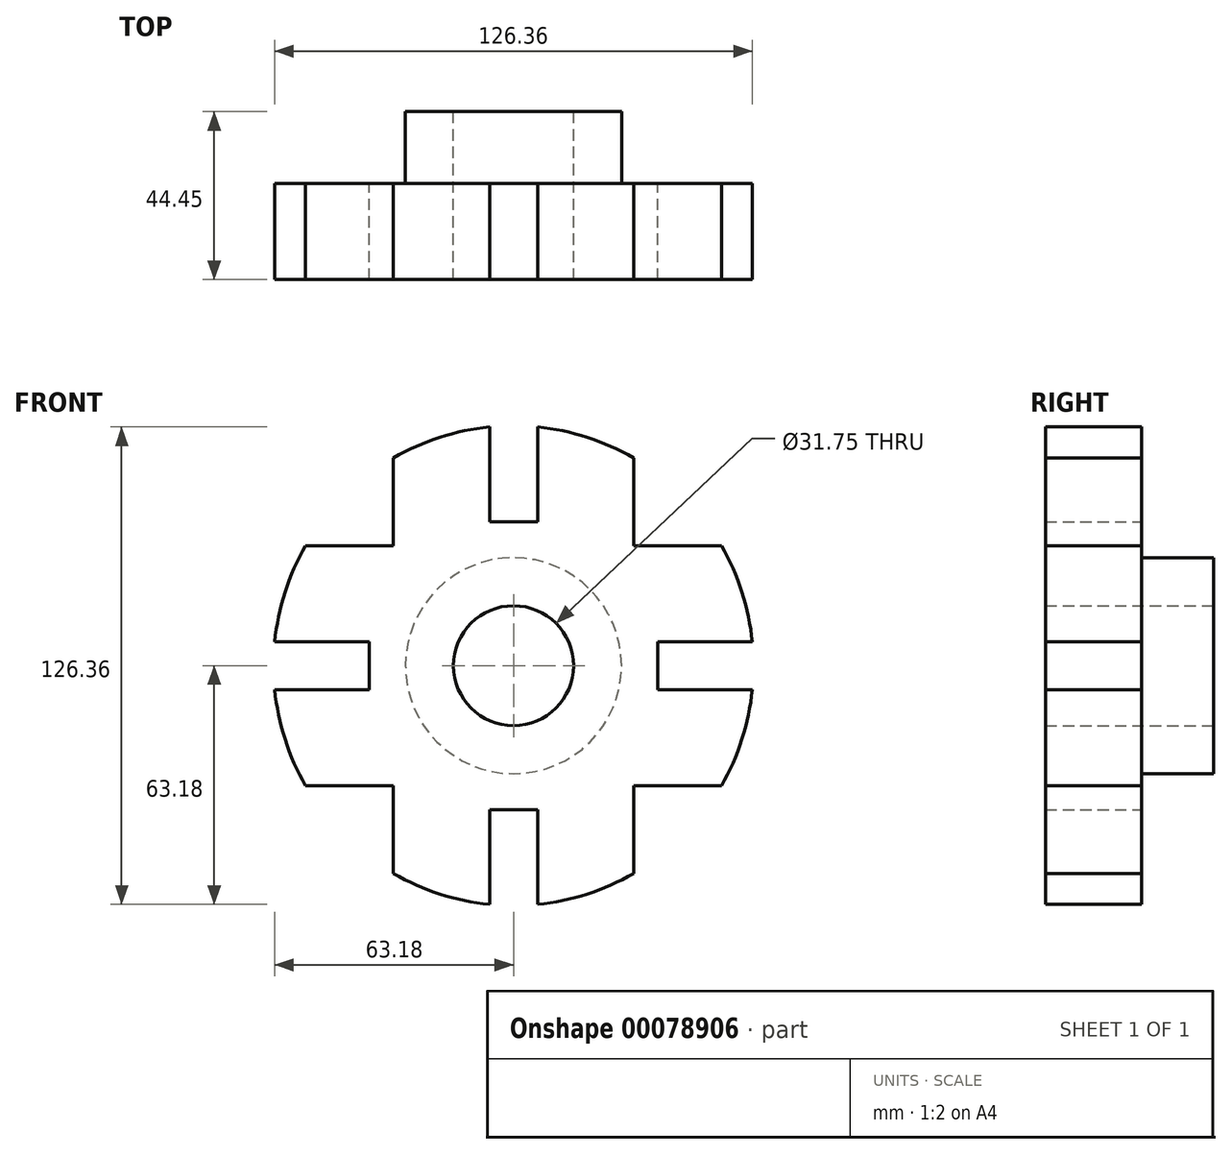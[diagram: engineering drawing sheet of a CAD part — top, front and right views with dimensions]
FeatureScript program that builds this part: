
annotation { "Feature Type Name" : "Feature", "Feature Type Description" : "" }
export const myFeature = defineFeature(function(context is Context, id is Id, definition is map)
    precondition{}
    {
        {
            var Q0;
            Q0=qCreatedBy(makeId("Front.planeOp"),FACE);
            var sketch = newSketch(context, id + "F0", { "sketchPlane" : qUnion([Q0])});
            skCircle(sketch, "E0", {"center": v(0, 0) * mm, "radius": 15.88 * mm});
            skCircle(sketch, "E1", {"center": v(0, 0) * mm, "radius": 28.58 * mm});
            skArc(sketch, "E2", {"start": v(63.18, 6.35) * mm, "mid": v(60.44, 19.49) * mm, "end": v(55, 31.75) * mm});
            skLineSegment(sketch, "E3", {"start": v(0, 38.1) * mm, "end": v(0, 0) * mm, "construction": true});
            skLineSegment(sketch, "E4", {"start": v(0, -28.58) * mm, "end": v(0, 0) * mm, "construction": true});
            skLineSegment(sketch, "E5", {"start": v(38.1, 0) * mm, "end": v(0, 0) * mm, "construction": true});
            skLineSegment(sketch, "E6", {"start": v(0, 0) * mm, "end": v(-28.58, 0) * mm, "construction": true});
            skLineSegment(sketch, "E7", {"start": v(0, 38.1) * mm, "end": v(6.35, 38.1) * mm});
            skLineSegment(sketch, "E8", {"start": v(6.35, 38.1) * mm, "end": v(6.35, 63.18) * mm});
            skLineSegment(sketch, "E9", {"start": v(31.75, 55) * mm, "end": v(31.75, 31.75) * mm});
            skLineSegment(sketch, "E10", {"start": v(31.75, 31.75) * mm, "end": v(55, 31.75) * mm});
            skLineSegment(sketch, "E11", {"start": v(38.1, 0) * mm, "end": v(38.1, 6.35) * mm});
            skLineSegment(sketch, "E12", {"start": v(38.1, 6.35) * mm, "end": v(63.18, 6.35) * mm});
            skPoint(sketch, "E13.orphan", {"position": v(0, -63.5) * mm});
            skArc(sketch, "E14.trimOffspring", {"start": v(31.75, 55) * mm, "mid": v(19.49, 60.44) * mm, "end": v(6.35, 63.18) * mm});
            skLineSegment(sketch, "E15.1.0", {"start": v(-38.1, 6.35) * mm, "end": v(-63.18, 6.35) * mm});
            skLineSegment(sketch, "E15.1.1", {"start": v(-55, 31.75) * mm, "end": v(-31.75, 31.75) * mm});
            skLineSegment(sketch, "E15.1.2", {"start": v(0, 38.1) * mm, "end": v(-6.35, 38.1) * mm});
            skLineSegment(sketch, "E15.1.3", {"start": v(-31.75, 31.75) * mm, "end": v(-31.75, 55) * mm});
            skArc(sketch, "E15.1.4", {"start": v(-6.35, 63.18) * mm, "mid": v(-19.49, 60.44) * mm, "end": v(-31.75, 55) * mm});
            skLineSegment(sketch, "E15.1.5", {"start": v(-6.35, 38.1) * mm, "end": v(-6.35, 63.18) * mm});
            skArc(sketch, "E15.1.6", {"start": v(-55, 31.75) * mm, "mid": v(-60.44, 19.49) * mm, "end": v(-63.18, 6.35) * mm});
            skLineSegment(sketch, "E15.1.7", {"start": v(-38.1, 0) * mm, "end": v(-38.1, 6.35) * mm});
            skLineSegment(sketch, "E15.2.0", {"start": v(-6.35, -38.1) * mm, "end": v(-6.35, -63.18) * mm});
            skLineSegment(sketch, "E15.2.1", {"start": v(-31.75, -55) * mm, "end": v(-31.75, -31.75) * mm});
            skLineSegment(sketch, "E15.2.2", {"start": v(-38.1, 0) * mm, "end": v(-38.1, -6.35) * mm});
            skLineSegment(sketch, "E15.2.3", {"start": v(-31.75, -31.75) * mm, "end": v(-55, -31.75) * mm});
            skArc(sketch, "E15.2.4", {"start": v(-63.18, -6.35) * mm, "mid": v(-60.44, -19.49) * mm, "end": v(-55, -31.75) * mm});
            skLineSegment(sketch, "E15.2.5", {"start": v(-38.1, -6.35) * mm, "end": v(-63.18, -6.35) * mm});
            skArc(sketch, "E15.2.6", {"start": v(-31.75, -55) * mm, "mid": v(-19.49, -60.44) * mm, "end": v(-6.35, -63.18) * mm});
            skLineSegment(sketch, "E15.2.7", {"start": v(0, -38.1) * mm, "end": v(-6.35, -38.1) * mm});
            skLineSegment(sketch, "E15.3.0", {"start": v(38.1, -6.35) * mm, "end": v(63.18, -6.35) * mm});
            skLineSegment(sketch, "E15.3.1", {"start": v(55, -31.75) * mm, "end": v(31.75, -31.75) * mm});
            skLineSegment(sketch, "E15.3.2", {"start": v(0, -38.1) * mm, "end": v(6.35, -38.1) * mm});
            skLineSegment(sketch, "E15.3.3", {"start": v(31.75, -31.75) * mm, "end": v(31.75, -55) * mm});
            skArc(sketch, "E15.3.4", {"start": v(6.35, -63.18) * mm, "mid": v(19.49, -60.44) * mm, "end": v(31.75, -55) * mm});
            skLineSegment(sketch, "E15.3.5", {"start": v(6.35, -38.1) * mm, "end": v(6.35, -63.18) * mm});
            skArc(sketch, "E15.3.6", {"start": v(55, -31.75) * mm, "mid": v(60.44, -19.49) * mm, "end": v(63.18, -6.35) * mm});
            skLineSegment(sketch, "E15.3.7", {"start": v(38.1, 0) * mm, "end": v(38.1, -6.35) * mm});
            skPoint(sketch, "E16.orphan", {"position": v(63.5, 0) * mm});
            skPoint(sketch, "E17.orphan", {"position": v(0, 63.5) * mm});
            skSolve(sketch);
        }
        {
            var Q0;
            Q0=makeQuery(id+"F0.imprint","IMPRINT",FACE,{"disambiguationData":[TD([[makeQuery(id+"F0.imprint","IMPRINT",EDGE,{"derivedFrom":sQuery(id+"F0.wireOp",EDGE,"E1")}),-1.0]])]});
            var Q1;
            Q1=makeQuery(id+"F0.imprint","IMPRINT",FACE,{"disambiguationData":[TD([[makeQuery(id+"F0.imprint","IMPRINT",EDGE,{"derivedFrom":sQuery(id+"F0.wireOp",EDGE,"E0")}),-1.0]])]});
            extrude(context, id + "F1", {"entities" : qUnion([Q0, Q1]), "depth" : 25.4 * mm});
        }
        {
            var Q0;
            Q0=makeQuery(id+"F0.imprint","IMPRINT",FACE,{"disambiguationData":[TD([[makeQuery(id+"F0.imprint","IMPRINT",EDGE,{"derivedFrom":sQuery(id+"F0.wireOp",EDGE,"E0")}),-1.0]])]});
            extrude(context, id + "F2", {"entities" : qUnion([Q0]), "operationType" : NewBodyOperationType.ADD, "oppositeDirection" : true, "depth" : 19.05 * mm});
        }
    });
